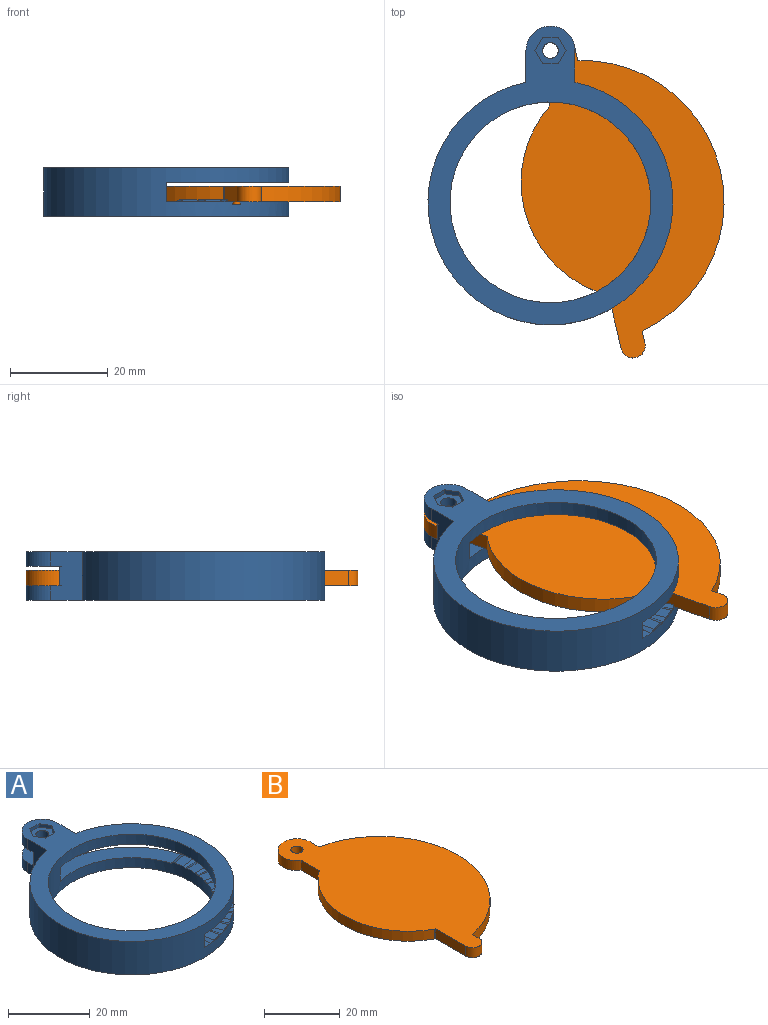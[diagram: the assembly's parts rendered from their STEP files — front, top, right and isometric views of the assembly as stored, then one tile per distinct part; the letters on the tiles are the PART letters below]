
ASSEMBLY  parts=2 mates=1
PART A: 75 faces, bbox 50x61x10 mm
  f0: plane 30.19x28.98mm, normal (0,0,1), area 236.1mm2, adj f12,f13,f14,f17,f18,f22,f23,f25
  f1: plane 4.79x0.92mm, normal (0,0,1), area 0.4mm2, adj f18,f70
  f2: plane 4.88x0.14mm, normal (0,0,1), area 0.4mm2, adj f18,f66
  f3: plane 4.78x0.98mm, normal (0,0,1), area 0.4mm2, adj f18,f62
  f4: plane 4.5x1.89mm, normal (0,0,1), area 0.4mm2, adj f18,f58
  f5: plane 4.05x2.73mm, normal (0,0,1), area 0.4mm2, adj f18,f54
  f6: plane 3.46x3.44mm, normal (0,0,1), area 0.4mm2, adj f18,f50
  f7: plane 4.07x2.7mm, normal (0,0,1), area 0.4mm2, adj f18,f46
  f8: plane 4.51x1.86mm, normal (0,0,1), area 0.4mm2, adj f18,f42
  f9: plane 4.79x0.95mm, normal (0,0,1), area 0.4mm2, adj f18,f37
  f10: plane 61x50mm, normal (0,0,1), area 718mm2, adj f16,f17,f18,f19,f22,f30,f31,f32
  f11: cylinder r=1.6mm len=3.2mm, axis (0,0,-1), area 20.1mm2, adj f24,f36
  f12: cylinder r=5mm len=10mm, axis (0,0,-1), area 47.1mm2, adj f0,f13,f17,f20
  f13: plane 6.51x3mm, normal (1,0,0), area 19.5mm2, adj f0,f12,f18,f20
  f14: cylinder r=25mm len=4mm, axis (0,0,-1), area 0.6mm2, adj f0,f23,f24,f26
  f15: plane 4.6x2.44mm, normal (0,0,1), area 10mm2, adj f18,f21,f22,f39
  f16: cylinder r=5mm len=10mm, axis (0,0,-1), area 47.1mm2, adj f10,f17,f19,f24
  f17: plane 10x6.51mm, normal (-1,0,0), area 58mm2, adj f0,f10,f12,f16,f18,f20,f24,f25
  f18: cylinder r=25mm len=50mm, axis (0,0,-1), area 1176.1mm2, adj f0,f1,f2,f3,f4,f5,f6,f7
  f19: plane 6.51x3mm, normal (1,0,0), area 19.5mm2, adj f10,f16,f18,f24
  f20: plane 61x50mm, normal (0,0,-1), area 715.9mm2, adj f12,f13,f17,f18,f22,f29
  f21: plane 4.5x4mm, normal (1,0,0), area 18mm2, adj f15,f18,f22,f24
  f22: cylinder r=20.5mm len=41mm, axis (0,0,-1), area 1023.2mm2, adj f0,f10,f15,f20,f21,f23,f24,f38
  f23: plane 4.94x4mm, normal (0.93,-0.38,0), area 21.3mm2, adj f0,f14,f22,f24
  f24: plane 61x30mm, normal (0,0,-1), area 426.4mm2, adj f11,f14,f16,f17,f18,f19,f21,f22
  f25: cylinder r=5.3mm len=4mm, axis (0,0,-1), area 14.1mm2, adj f0,f17,f24,f26
  f26: plane 4x1.69mm, normal (1,0,0), area 6.8mm2, adj f0,f14,f24,f25
  f27: cylinder r=1.6mm len=3.2mm, axis (0,0,-1), area 20.1mm2, adj f0,f28
  f28: plane 6x6mm, normal (0,0,-1), area 20.2mm2, adj f27,f29
  f29: cylinder r=3mm len=6mm, axis (0,0,-1), area 18.8mm2, adj f20,f28
  f30: plane 2.75x1.59mm, normal (-0.87,0.5,0), area 3.2mm2, adj f10,f31,f35,f36
  f31: plane 2.75x1.59mm, normal (-0.87,-0.5,0), area 3.2mm2, adj f10,f30,f32,f36
  f32: plane 3.18x1mm, normal (0,-1,0), area 3.2mm2, adj f10,f31,f33,f36
  f33: plane 2.75x1.59mm, normal (0.87,-0.5,0), area 3.2mm2, adj f10,f32,f34,f36
  f34: plane 2.75x1.59mm, normal (0.87,0.5,0), area 3.2mm2, adj f10,f33,f35,f36
  f35: plane 3.18x1mm, normal (0,1,0), area 3.2mm2, adj f10,f30,f34,f36
  f36: plane 6.35x5.5mm, normal (0,0,1), area 18.2mm2, adj f11,f30,f31,f32,f33,f34,f35
  f37: plane 4.79x0.95mm, normal (0.19,-0.98,0), area 1.5mm2, adj f9,f38,f40,f41
  f38: plane 4.86x3.49mm, normal (0,0,1), area 11.8mm2, adj f22,f37,f40,f41
  f39: plane 4.48x0.44mm, normal (-1,-0.1,0), area 0.4mm2, adj f15,f22,f41
  f40: plane 4.53x1.95mm, normal (0.34,0.07,0.94), area 4.2mm2, adj f22,f37,f38,f45
  f41: plane 4.55x1.52mm, normal (-0.34,-0.07,0.94), area 4.2mm2, adj f22,f37,f38,f39
  f42: plane 4.51x1.86mm, normal (0.38,-0.92,0), area 1.5mm2, adj f8,f43,f44,f45
  f43: plane 5.11x4.16mm, normal (0,0,1), area 11.8mm2, adj f22,f42,f44,f45
  f44: plane 4.4x2.71mm, normal (0.32,0.13,0.94), area 4.2mm2, adj f22,f42,f43,f49
  f45: plane 4.51x2.32mm, normal (-0.32,-0.13,0.94), area 4.2mm2, adj f22,f40,f42,f43
  f46: plane 4.07x2.7mm, normal (0.55,-0.83,0), area 1.5mm2, adj f7,f47,f48,f49
  f47: plane 5.17x4.68mm, normal (0,0,1), area 11.8mm2, adj f22,f46,f48,f49
  f48: plane 4.1x3.37mm, normal (0.28,0.19,0.94), area 4.2mm2, adj f22,f46,f47,f53
  f49: plane 4.3x3.03mm, normal (-0.28,-0.19,0.94), area 4.2mm2, adj f22,f44,f46,f47
  f50: plane 3.46x3.44mm, normal (0.7,-0.71,0), area 1.5mm2, adj f6,f51,f52,f53
  f51: plane 5.03x5.02mm, normal (0,0,1), area 11.8mm2, adj f22,f50,f52,f53
  f52: plane 3.9x3.65mm, normal (0.24,0.24,0.94), area 4.2mm2, adj f22,f50,f51,f57
  f53: plane 3.92x3.63mm, normal (-0.24,-0.24,0.94), area 4.2mm2, adj f22,f48,f50,f51
  f54: plane 4.05x2.73mm, normal (0.83,-0.56,0), area 1.5mm2, adj f5,f55,f56,f57
  f55: plane 5.17x4.7mm, normal (0,0,1), area 11.8mm2, adj f22,f54,f56,f57
  f56: plane 4.29x3.06mm, normal (0.19,0.28,0.94), area 4.2mm2, adj f22,f54,f55,f61
  f57: plane 4.09x3.39mm, normal (-0.19,-0.28,0.94), area 4.2mm2, adj f22,f52,f54,f55
  f58: plane 4.5x1.89mm, normal (0.92,-0.39,0), area 1.5mm2, adj f4,f59,f60,f61
  f59: plane 5.12x4.18mm, normal (0,0,1), area 11.8mm2, adj f22,f58,f60,f61
  f60: plane 4.51x2.35mm, normal (0.13,0.32,0.94), area 4.2mm2, adj f22,f58,f59,f65
  f61: plane 4.39x2.73mm, normal (-0.13,-0.32,0.94), area 4.2mm2, adj f22,f56,f58,f59
  f62: plane 4.78x0.98mm, normal (0.98,-0.2,0), area 1.5mm2, adj f3,f63,f64,f65
  f63: plane 4.87x3.51mm, normal (0,0,1), area 11.8mm2, adj f22,f62,f64,f65
  f64: plane 4.56x1.55mm, normal (0.07,0.34,0.94), area 4.2mm2, adj f22,f62,f63,f69
  f65: plane 4.52x1.97mm, normal (-0.07,-0.34,0.94), area 4.2mm2, adj f22,f60,f62,f63
  f66: plane 4.88x0.4mm, normal (1,-0.01,0), area 1.5mm2, adj f2,f67,f68,f69
  f67: plane 4.44x2.71mm, normal (0,0,1), area 11.8mm2, adj f22,f66,f68,f69
  f68: plane 4.48x1.11mm, normal (0,0.34,0.94), area 4.2mm2, adj f22,f66,f67,f74
  f69: plane 4.49x1.13mm, normal (0,-0.34,0.94), area 4.2mm2, adj f22,f64,f66,f67
  f70: plane 4.79x0.92mm, normal (0.98,0.19,0), area 1.5mm2, adj f1,f72,f73,f74
  f71: plane 4.32x1.28mm, normal (-0.28,0.96,0), area 0.4mm2, adj f0,f22,f73
  f72: plane 4.85x3.47mm, normal (0,0,1), area 11.8mm2, adj f22,f70,f73,f74
  f73: plane 4.52x1.91mm, normal (-0.06,0.34,0.94), area 4.2mm2, adj f22,f70,f71,f72
  f74: plane 4.56x1.5mm, normal (0.06,-0.34,0.94), area 4.2mm2, adj f22,f68,f70,f72
PART B: 16 faces, bbox 40.8x70x3.7 mm
  f0: cylinder r=5mm len=10mm, axis (0,0,-1), area 66.3mm2, adj f1,f8,f9,f10
  f1: plane 6.77x3.2mm, normal (-1,0,0), area 21.7mm2, adj f0,f2,f9,f10
  f2: cylinder r=23.79mm len=40.22mm, axis (0,0,-1), area 153.9mm2, adj f1,f3,f9,f10
  f3: plane 3.2x0.3mm, normal (0,-1,0), area 1mm2, adj f2,f4,f9,f10
  f4: plane 11.3x3.2mm, normal (-1,0,0), area 36.2mm2, adj f3,f5,f9,f10
  f5: cylinder r=2.5mm len=5mm, axis (0,0,-1), area 25.1mm2, adj f4,f6,f9,f10
  f6: plane 3.2x2.5mm, normal (1,0,0), area 8mm2, adj f5,f7,f9,f10
  f7: cylinder r=28.97mm len=56.75mm, axis (0,0,-1), area 253.5mm2, adj f6,f8,f9,f10
  f8: plane 3.25x3.2mm, normal (1,0,0), area 10.4mm2, adj f0,f7,f9,f10
  f9: plane 70x40.78mm, normal (0,0,1), area 1748.2mm2, adj f0,f1,f2,f3,f4,f5,f6,f7
  f10: plane 70x40.78mm, normal (0,0,-1), area 1744.7mm2, adj f0,f1,f2,f3,f4,f5,f6,f7
  f11: cylinder r=1.6mm len=3.2mm, axis (0,0,-1), area 32.2mm2, adj f9,f10
  f12: cylinder r=0.75mm len=1.5mm, axis (0,0,1), area 2.4mm2, adj f10,f13
  f13: plane 1.5x1.5mm, normal (0,0,-1), area 1.8mm2, adj f12
  f14: cylinder r=0.75mm len=1.5mm, axis (0,0,1), area 2.4mm2, adj f10,f15
  f15: plane 1.5x1.5mm, normal (0,0,-1), area 1.8mm2, adj f14
PLACE A at identity fixed
PLACE B rot(axis=(0,0,1),13.1deg) t=(7,0.8,0)mm
MATE revolute A.f11 <-> B.f11  axis (0,0,1) through (0,31,3)mm
